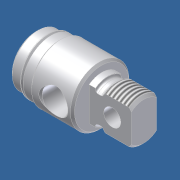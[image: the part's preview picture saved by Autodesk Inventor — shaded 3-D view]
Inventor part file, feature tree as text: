
AUTODESK INVENTOR PART (.ipt)
format: ipt  version: 2012 (Build 160160000, 160)  size: 266,752 bytes
history: native  units: in
note: dims shown in document units (in); Inventor stores cm internally (conversion verified against a paired STEP export)
features: other x155, sketch x7, revolve x5, extrude x2, thread x1
ambient origin geometry x8: Origin, YZ Plane, XZ Plane, XY Plane, X Axis, Y Axis, Z Axis, Center Point
bodies: Solid1 (feature_tree)
feature tree (170):
  other  "04P0010_rear_head"
  revolve  "Revolution1"  Angle=360.0deg
  revolve  "Revolution2"  [1 undecoded]
  thread  "Thread1"  [1 undecoded]
  extrude  "Extrusion1"  TaperAngle=360.0deg  [1 undecoded]
  revolve  "Revolution3"  [1 undecoded]
  revolve  "Revolution4"  [1 undecoded]
  revolve  "Revolution5"  [1 undecoded]
  extrude  "Extrusion2"  [1 undecoded]
  other  "c1_XY"
  other  "c1_YZ"
  other  "c1_ZX"
  other  "c1_X"
  other  "c1_Y"
  other  "c1_Z"
  other  "c1_Center"
  other  "cc1_XY"
  other  "cc1_YZ"
  other  "cc1_ZX"
  other  "cc1_X"
  other  "cc1_Y"
  other  "cc1_Z"
  other  "cc1_Center"
  other  "c2_XY"
  other  "c2_YZ"
  other  "c2_ZX"
  other  "c2_X"
  other  "c2_Y"
  other  "c2_Z"
  other  "c2_Center"
  other  "cc2_XY"
  other  "cc2_YZ"
  other  "cc2_ZX"
  other  "cc2_X"
  other  "cc2_Y"
  other  "cc2_Z"
  other  "cc2_Center"
  other  "to_tube_XY"
  other  "to_tube_YZ"
  other  "to_tube_ZX"
  other  "to_tube_X"
  other  "to_tube_Y"
  other  "to_tube_Z"
  other  "to_tube_Center"
  other  "to_nut_XY"
  other  "to_nut_YZ"
  other  "to_nut_ZX"
  other  "to_nut_X"
  other  "to_nut_Y"
  other  "to_nut_Z"
  other  "to_nut_Center"
  other  "lovra1_XY"
  other  "lovra1_YZ"
  other  "lovra1_ZX"
  other  "lovra1_X"
  other  "lovra1_Y"
  other  "lovra1_Z"
  other  "lovra1_Center"
  other  "lovra2_XY"
  other  "lovra2_YZ"
  other  "lovra2_ZX"
  other  "lovra2_X"
  other  "lovra2_Y"
  other  "lovra2_Z"
  other  "lovra2_Center"
  other  "lovra3_XY"
  other  "lovra3_YZ"
  other  "lovra3_ZX"
  other  "lovra3_X"
  other  "lovra3_Y"
  other  "lovra3_Z"
  other  "lovra3_Center"
  other  "to_pin_XY"
  other  "to_pin_YZ"
  other  "to_pin_ZX"
  other  "to_pin_X"
  other  "to_pin_Y"
  other  "to_pin_Z"
  other  "to_pin_Center"
  other  "olen_XY"
  other  "olen_YZ"
  other  "olen_ZX"
  other  "olen_X"
  other  "olen_Y"
  other  "olen_Z"
  other  "olen_Center"
  other  "thd1_XY"
  other  "thd1_YZ"
  other  "thd1_ZX"
  other  "thd1_X"
  other  "thd1_Y"
  other  "thd1_Z"
  other  "thd1_Center"
  other  "p1_XY"
  other  "p1_YZ"
  other  "p1_ZX"
  other  "p1_X"
  other  "p1_Y"
  other  "p1_Z"
  other  "p1_Center"
  other  "thd2_XY"
  other  "thd2_YZ"
  other  "thd2_ZX"
  other  "thd2_X"
  other  "thd2_Y"
  other  "thd2_Z"
  other  "thd2_Center"
  other  "p2_XY"
  other  "p2_YZ"
  other  "p2_ZX"
  other  "p2_X"
  other  "p2_Y"
  other  "p2_Z"
  other  "p2_Center"
  other  "port2_XY"
  other  "port2_YZ"
  other  "port2_ZX"
  other  "port2_X"
  other  "port2_Y"
  other  "port2_Z"
  other  "port2_Center"
  other  "port_XY"
  other  "port_YZ"
  other  "port_ZX"
  other  "port_X"
  other  "port_Y"
  other  "port_Z"
  other  "port_Center"
  other  "1_XY"
  other  "1_YZ"
  other  "1_ZX"
  other  "1_X"
  other  "1_Y"
  other  "1_Z"
  other  "1_Center"
  other  "lovra21_XY"
  other  "lovra21_YZ"
  other  "lovra21_ZX"
  other  "lovra21_X"
  other  "lovra21_Y"
  other  "lovra21_Z"
  other  "lovra21_Center"
  other  "lovra22_XY"
  other  "lovra22_YZ"
  other  "lovra22_ZX"
  other  "lovra22_X"
  other  "lovra22_Y"
  other  "lovra22_Z"
  other  "lovra22_Center"
  other  "to_screw_XY"
  other  "to_screw_YZ"
  other  "to_screw_ZX"
  other  "to_screw_X"
  other  "to_screw_Y"
  other  "to_screw_Z"
  other  "to_screw_Center"
  other  "to_mounting_bracket_XY"
  other  "to_mounting_bracket_YZ"
  other  "to_mounting_bracket_ZX"
  other  "to_mounting_bracket_X"
  other  "to_mounting_bracket_Y"
  other  "to_mounting_bracket_Z"
  other  "to_mounting_bracket_Center"
  sketch  "Sketch_8"  dims[d0=360.0deg d1=360.0deg]
  sketch  "Sketch_15"  dims[d9=0.5587in d10=0.0in]
  sketch  "Sketch_9"  dims[d2=0.4208in d3=0.0in d4=0.625in d5=0.0in d6=360.0deg]
  sketch  "Sketch_13"  dims[d7=360.0deg d8=360.0deg]
  sketch  "Sketch_19"
  sketch  "Sketch_24"
  sketch  "Sketch_43"
note: 7 required parameter values undecoded (feature->parameter linkage not recoverable at this tier; creation-order binding heuristic only, values carry confidence <= 0.55)